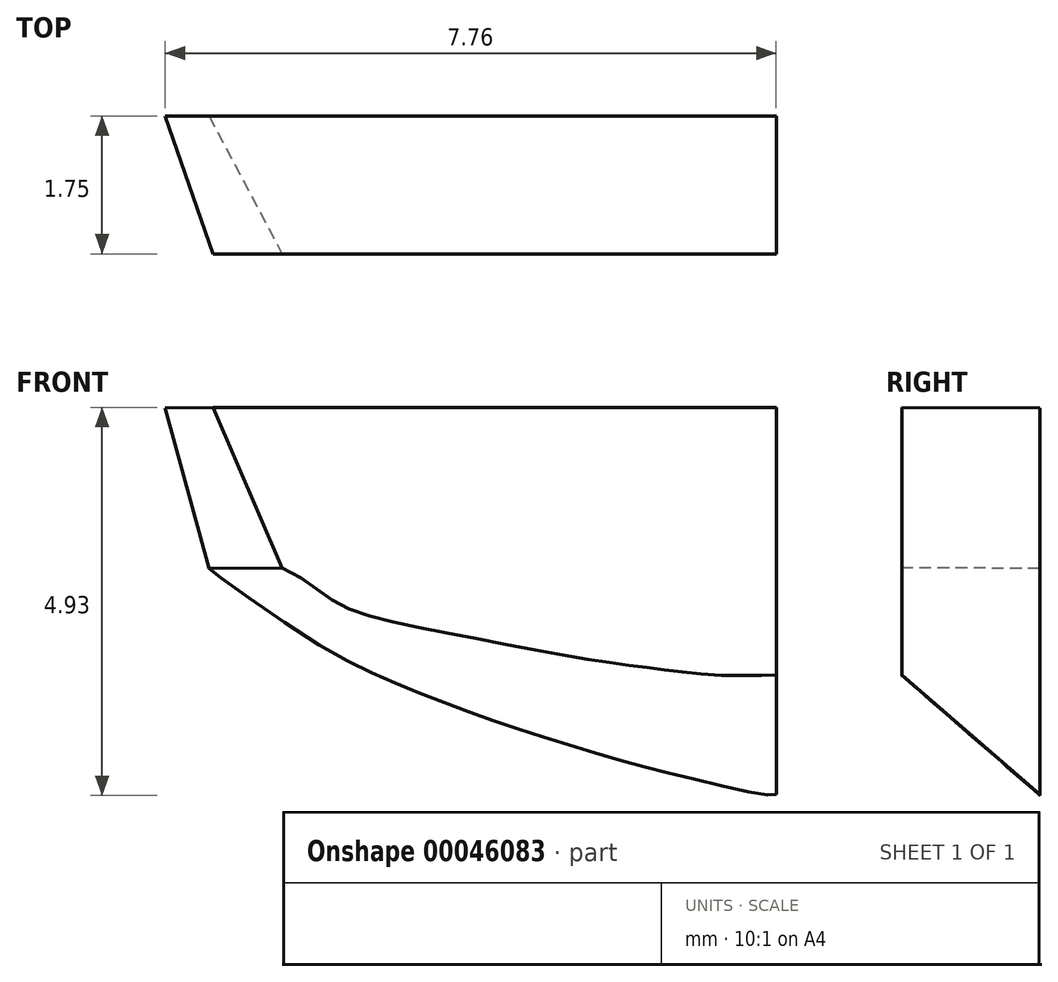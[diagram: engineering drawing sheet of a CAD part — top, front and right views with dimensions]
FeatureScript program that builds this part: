
annotation { "Feature Type Name" : "Feature", "Feature Type Description" : "" }
export const myFeature = defineFeature(function(context is Context, id is Id, definition is map)
    precondition{}
    {
        {
            var Q0;
            Q0=qCreatedBy(makeId("Front.planeOp"),FACE);
            cPlane(context, id + "F0", {"entities" : qUnion([Q0]), "cplaneType" : CPlaneType.OFFSET, "offset" : 1.75 * mm, "width" : 152.4 * mm, "height" : 152.4 * mm});
        }
        {
            var Q0;
            Q0=qCreatedBy(makeId("Front.planeOp"),FACE);
            var sketch = newSketch(context, id + "F1", { "sketchPlane" : qUnion([Q0])});
            skFitSpline(sketch, "E0", {"points": [v(3.77, -3.1) * mm, v(3.65, -3.1) * mm, v(2.73, -2.9) * mm, v(1.84, -2.68) * mm, v(0.84, -2.37) * mm, v(-0.1, -2.07) * mm, v(-1.05, -1.7) * mm, v(-2.13, -1.14) * mm, v(-3.43, -0.22) * mm, v(-3.43, -0.22) * mm], "startDerivative": vector(-2.1, -0.37) * mm, "endDerivative": vector(0.17, 0.27) * mm});
            skLineSegment(sketch, "E1", {"start": v(-3.43, -0.22) * mm, "end": v(-4, 1.81) * mm});
            skLineSegment(sketch, "E2", {"start": v(-4, 1.81) * mm, "end": v(3.77, 1.81) * mm});
            skLineSegment(sketch, "E3", {"start": v(3.77, 1.81) * mm, "end": v(3.77, -3.1) * mm});
            skSolve(sketch);
        }
        {
            var Q0;
            Q0=qCreatedBy(id+"F0.planeOp",FACE);
            var sketch = newSketch(context, id + "F2", { "sketchPlane" : qUnion([Q0])});
            skLineSegment(sketch, "E4", {"start": v(-2.5, -0.22) * mm, "end": v(-3.38, 1.82) * mm});
            skLineSegment(sketch, "E5", {"start": v(-3.38, 1.82) * mm, "end": v(3.77, 1.82) * mm});
            skLineSegment(sketch, "E6", {"start": v(3.77, 1.82) * mm, "end": v(3.77, -1.58) * mm});
            skFitSpline(sketch, "E7", {"points": [v(3.77, -1.58) * mm, v(3, -1.58) * mm, v(2.22, -1.5) * mm, v(1.35, -1.37) * mm, v(-0.5, -1.03) * mm, v(-1.77, -0.68) * mm, v(-2.5, -0.22) * mm], "startDerivative": vector(-3.34, -0.12) * mm, "endDerivative": vector(-6.21, 2.71) * mm});
            skSolve(sketch);
        }
        {
            var Q0;
            {var subQ0=sQuery(id+"F1.wireOp",EDGE,"E2");Q0=makeQuery(id+"F1.imprint","IMPRINT",FACE,{"disambiguationData":[TD([[makeQuery(id+"F1.imprint","IMPRINT",EDGE,{"derivedFrom":subQ0}),-1.0]])]});}
            var Q1;
            Q1=makeQuery(id+"F2.imprint","IMPRINT",FACE,{"disambiguationData":[TD([[makeQuery(id+"F2.imprint","IMPRINT",EDGE,{"derivedFrom":sQuery(id+"F2.wireOp",EDGE,"E4")}),-1.0]])]});
            var Q2;
            Q2=sQuery(id+"F2.wireOp",VERTEX,"E5.start");
            var Q3;
            Q3=sQuery(id+"F1.wireOp",VERTEX,"E2.start");
            loft(context, id + "F3", {"sheetProfilesArray" : [{ "sheetProfileEntities" : qUnion([Q0]) }, { "sheetProfileEntities" : qUnion([Q1]) }], "matchConnections" : true, "connections" : [{ "connectionEntities" : qUnion([Q2, Q3]), "connectionEdgeQueries" : qUnion([]), "connectionEdgeParameters" : [] }]});
        }
    });
